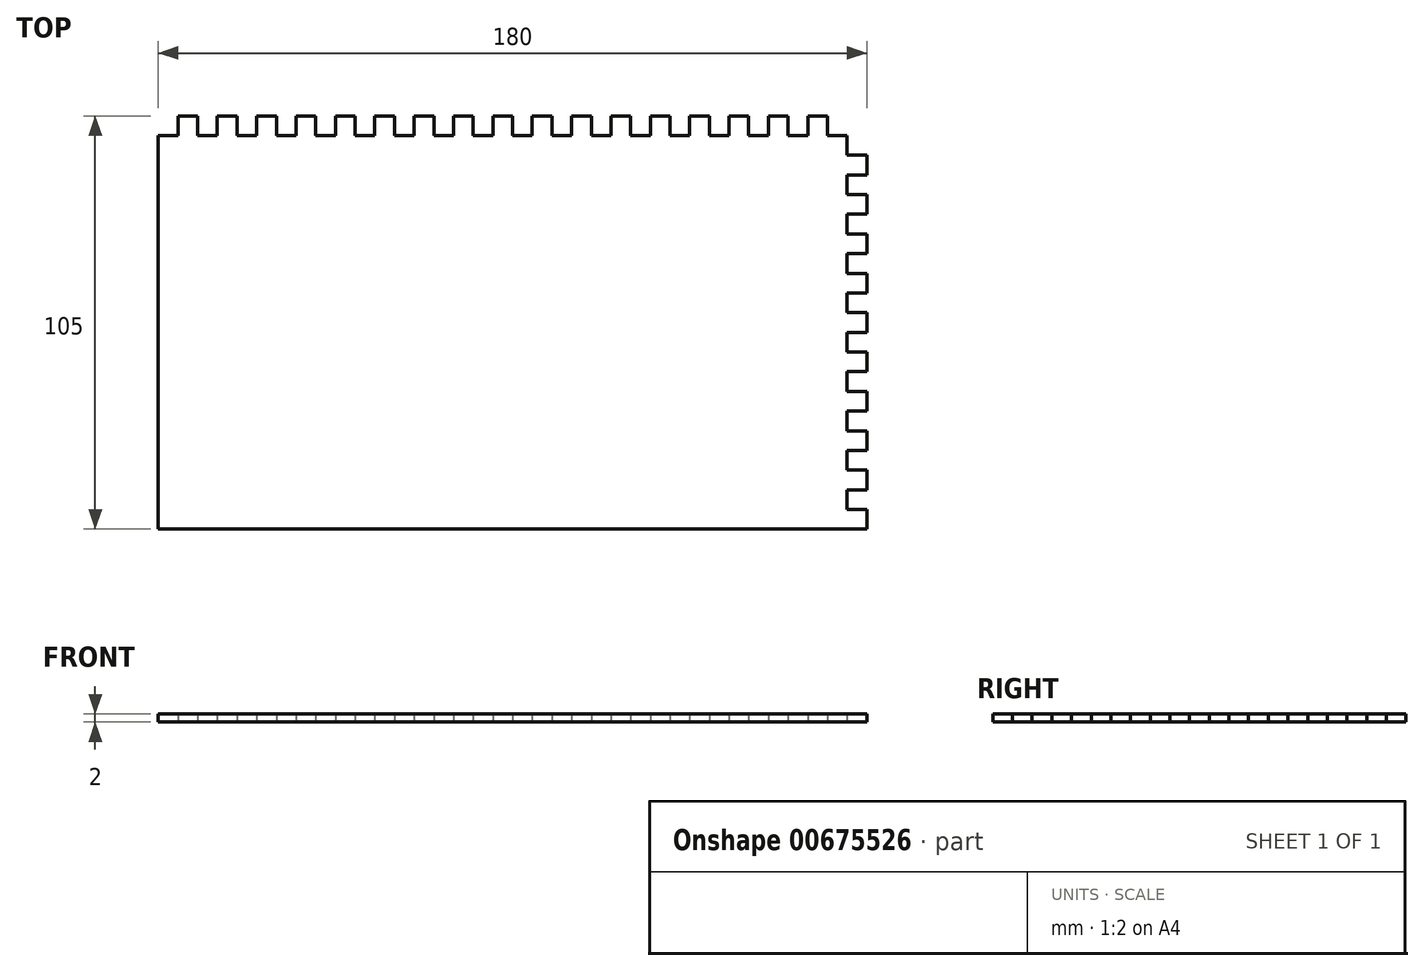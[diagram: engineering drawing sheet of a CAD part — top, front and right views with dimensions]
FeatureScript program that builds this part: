
annotation { "Feature Type Name" : "Feature", "Feature Type Description" : "" }
export const myFeature = defineFeature(function(context is Context, id is Id, definition is map)
    precondition{}
    {
        {
            var Q0;
            Q0=qCreatedBy(makeId("Top.planeOp"),FACE);
            var sketch = newSketch(context, id + "F0", { "sketchPlane" : qUnion([Q0])});
            skLineSegment(sketch, "E0", {"start": v(-180, -103.5) * mm, "end": v(-5, -103.5) * mm});
            skLineSegment(sketch, "E1", {"start": v(-180, -3.5) * mm, "end": v(-180, -103.5) * mm});
            skLineSegment(sketch, "E2", {"start": v(-175, 1.5) * mm, "end": v(-175, -3.5) * mm});
            skLineSegment(sketch, "E3", {"start": v(-170, 1.5) * mm, "end": v(-170, -3.5) * mm});
            skLineSegment(sketch, "E4", {"start": v(-165, 1.5) * mm, "end": v(-165, -3.5) * mm});
            skLineSegment(sketch, "E5", {"start": v(-160, 1.5) * mm, "end": v(-160, -3.5) * mm});
            skLineSegment(sketch, "E6", {"start": v(-155, 1.5) * mm, "end": v(-155, -3.5) * mm});
            skLineSegment(sketch, "E7", {"start": v(-150, 1.5) * mm, "end": v(-150, -3.5) * mm});
            skLineSegment(sketch, "E8", {"start": v(-145, 1.5) * mm, "end": v(-145, -3.5) * mm});
            skLineSegment(sketch, "E9", {"start": v(-140, 1.5) * mm, "end": v(-140, -3.5) * mm});
            skLineSegment(sketch, "E10", {"start": v(-135, 1.5) * mm, "end": v(-135, -3.5) * mm});
            skLineSegment(sketch, "E11", {"start": v(-130, 1.5) * mm, "end": v(-130, -3.5) * mm});
            skLineSegment(sketch, "E12", {"start": v(-125, 1.5) * mm, "end": v(-125, -3.5) * mm});
            skLineSegment(sketch, "E13", {"start": v(-85, 1.5) * mm, "end": v(-85, -3.5) * mm});
            skLineSegment(sketch, "E14", {"start": v(-80, 1.5) * mm, "end": v(-80, -3.5) * mm});
            skLineSegment(sketch, "E15", {"start": v(-75, 1.5) * mm, "end": v(-75, -3.5) * mm});
            skLineSegment(sketch, "E16", {"start": v(-70, 1.5) * mm, "end": v(-70, -3.5) * mm});
            skLineSegment(sketch, "E17", {"start": v(-65, 1.5) * mm, "end": v(-65, -3.5) * mm});
            skLineSegment(sketch, "E18", {"start": v(-60, 1.5) * mm, "end": v(-60, -3.5) * mm});
            skLineSegment(sketch, "E19", {"start": v(-55, 1.5) * mm, "end": v(-55, -3.5) * mm});
            skLineSegment(sketch, "E20", {"start": v(-50, 1.5) * mm, "end": v(-50, -3.5) * mm});
            skLineSegment(sketch, "E21", {"start": v(-45, 1.5) * mm, "end": v(-45, -3.5) * mm});
            skLineSegment(sketch, "E22", {"start": v(-40, 1.5) * mm, "end": v(-40, -3.5) * mm});
            skLineSegment(sketch, "E23", {"start": v(-35, 1.5) * mm, "end": v(-35, -3.5) * mm});
            skLineSegment(sketch, "E24", {"start": v(-30, 1.5) * mm, "end": v(-30, -3.5) * mm});
            skLineSegment(sketch, "E25", {"start": v(-25, 1.5) * mm, "end": v(-25, -3.5) * mm});
            skLineSegment(sketch, "E26", {"start": v(-20, 1.5) * mm, "end": v(-20, -3.5) * mm});
            skLineSegment(sketch, "E27", {"start": v(-15, 1.5) * mm, "end": v(-15, -3.5) * mm});
            skLineSegment(sketch, "E28", {"start": v(-10, 1.5) * mm, "end": v(-10, -3.5) * mm});
            skLineSegment(sketch, "E29", {"start": v(-5, -3.5) * mm, "end": v(-5, -8.5) * mm});
            skLineSegment(sketch, "E30", {"start": v(-5, -8.5) * mm, "end": v(0, -8.5) * mm});
            skLineSegment(sketch, "E31", {"start": v(-5, -13.5) * mm, "end": v(0, -13.5) * mm});
            skLineSegment(sketch, "E32", {"start": v(-5, -18.5) * mm, "end": v(0, -18.5) * mm});
            skLineSegment(sketch, "E33", {"start": v(0, -23.5) * mm, "end": v(-5, -23.5) * mm});
            skLineSegment(sketch, "E34", {"start": v(-5, -28.5) * mm, "end": v(0, -28.5) * mm});
            skLineSegment(sketch, "E35", {"start": v(-5, -33.5) * mm, "end": v(0, -33.5) * mm});
            skLineSegment(sketch, "E36", {"start": v(0, -38.5) * mm, "end": v(-5, -38.5) * mm});
            skLineSegment(sketch, "E37", {"start": v(-5, -43.5) * mm, "end": v(0, -43.5) * mm});
            skLineSegment(sketch, "E38", {"start": v(0, -48.5) * mm, "end": v(-5, -48.5) * mm});
            skLineSegment(sketch, "E39", {"start": v(-5, -53.5) * mm, "end": v(0, -53.5) * mm});
            skLineSegment(sketch, "E40", {"start": v(0, -58.5) * mm, "end": v(-5, -58.5) * mm});
            skLineSegment(sketch, "E41", {"start": v(-5, -63.5) * mm, "end": v(0, -63.5) * mm});
            skLineSegment(sketch, "E42", {"start": v(-5, -68.5) * mm, "end": v(0, -68.5) * mm});
            skLineSegment(sketch, "E43", {"start": v(-5, -73.5) * mm, "end": v(0, -73.5) * mm});
            skLineSegment(sketch, "E44", {"start": v(-5, -78.5) * mm, "end": v(0, -78.5) * mm});
            skLineSegment(sketch, "E45", {"start": v(-5, -83.5) * mm, "end": v(0, -83.5) * mm});
            skLineSegment(sketch, "E46", {"start": v(-5, -88.5) * mm, "end": v(0, -88.5) * mm});
            skLineSegment(sketch, "E47", {"start": v(-5, -93.5) * mm, "end": v(0, -93.5) * mm});
            skLineSegment(sketch, "E48", {"start": v(-5, -98.5) * mm, "end": v(0, -98.5) * mm});
            skLineSegment(sketch, "E49", {"start": v(-120, -3.5) * mm, "end": v(-120, 1.5) * mm});
            skLineSegment(sketch, "E50", {"start": v(-115, 1.5) * mm, "end": v(-115, -3.5) * mm});
            skLineSegment(sketch, "E51", {"start": v(-110, -3.5) * mm, "end": v(-110, 1.5) * mm});
            skLineSegment(sketch, "E52", {"start": v(-105, 1.5) * mm, "end": v(-105, -3.5) * mm});
            skLineSegment(sketch, "E53", {"start": v(-100, 1.5) * mm, "end": v(-100, -3.5) * mm});
            skLineSegment(sketch, "E54", {"start": v(-95, 1.5) * mm, "end": v(-95, -3.5) * mm});
            skLineSegment(sketch, "E55", {"start": v(-90, 1.5) * mm, "end": v(-90, -3.5) * mm});
            skLineSegment(sketch, "E56", {"start": v(-175, 1.5) * mm, "end": v(-170, 1.5) * mm});
            skLineSegment(sketch, "E57", {"start": v(-175, -3.5) * mm, "end": v(-180, -3.5) * mm});
            skLineSegment(sketch, "E58", {"start": v(-170, -3.5) * mm, "end": v(-165, -3.5) * mm});
            skLineSegment(sketch, "E59", {"start": v(-160, 1.5) * mm, "end": v(-165, 1.5) * mm});
            skLineSegment(sketch, "E60", {"start": v(-155, 1.5) * mm, "end": v(-150, 1.5) * mm});
            skLineSegment(sketch, "E61", {"start": v(-145, 1.5) * mm, "end": v(-140, 1.5) * mm});
            skLineSegment(sketch, "E62", {"start": v(-135, 1.5) * mm, "end": v(-130, 1.5) * mm});
            skLineSegment(sketch, "E63", {"start": v(-125, 1.5) * mm, "end": v(-120, 1.5) * mm});
            skLineSegment(sketch, "E64", {"start": v(-125, -3.5) * mm, "end": v(-130, -3.5) * mm});
            skLineSegment(sketch, "E65", {"start": v(-135, -3.5) * mm, "end": v(-140, -3.5) * mm});
            skLineSegment(sketch, "E66", {"start": v(-145, -3.5) * mm, "end": v(-150, -3.5) * mm});
            skLineSegment(sketch, "E67", {"start": v(-155, -3.5) * mm, "end": v(-160, -3.5) * mm});
            skLineSegment(sketch, "E68", {"start": v(-120, -3.5) * mm, "end": v(-115, -3.5) * mm});
            skLineSegment(sketch, "E69", {"start": v(-115, 1.5) * mm, "end": v(-110, 1.5) * mm});
            skLineSegment(sketch, "E70", {"start": v(-110, -3.5) * mm, "end": v(-105, -3.5) * mm});
            skLineSegment(sketch, "E71", {"start": v(-105, 1.5) * mm, "end": v(-100, 1.5) * mm});
            skLineSegment(sketch, "E72", {"start": v(-100, -3.5) * mm, "end": v(-95, -3.5) * mm});
            skLineSegment(sketch, "E73", {"start": v(-95, 1.5) * mm, "end": v(-90, 1.5) * mm});
            skLineSegment(sketch, "E74", {"start": v(-90, -3.5) * mm, "end": v(-85, -3.5) * mm});
            skLineSegment(sketch, "E75", {"start": v(-85, 1.5) * mm, "end": v(-80, 1.5) * mm});
            skLineSegment(sketch, "E76", {"start": v(-80, -3.5) * mm, "end": v(-75, -3.5) * mm});
            skLineSegment(sketch, "E77", {"start": v(-75, 1.5) * mm, "end": v(-70, 1.5) * mm});
            skLineSegment(sketch, "E78", {"start": v(-70, -3.5) * mm, "end": v(-65, -3.5) * mm});
            skLineSegment(sketch, "E79", {"start": v(-65, 1.5) * mm, "end": v(-60, 1.5) * mm});
            skLineSegment(sketch, "E80", {"start": v(-60, -3.5) * mm, "end": v(-55, -3.5) * mm});
            skLineSegment(sketch, "E81", {"start": v(-55, 1.5) * mm, "end": v(-50, 1.5) * mm});
            skLineSegment(sketch, "E82", {"start": v(-50, -3.5) * mm, "end": v(-45, -3.5) * mm});
            skLineSegment(sketch, "E83", {"start": v(-45, 1.5) * mm, "end": v(-40, 1.5) * mm});
            skLineSegment(sketch, "E84", {"start": v(-40, -3.5) * mm, "end": v(-35, -3.5) * mm});
            skLineSegment(sketch, "E85", {"start": v(-35, 1.5) * mm, "end": v(-30, 1.5) * mm});
            skLineSegment(sketch, "E86", {"start": v(-30, -3.5) * mm, "end": v(-25, -3.5) * mm});
            skLineSegment(sketch, "E87", {"start": v(-25, 1.5) * mm, "end": v(-20, 1.5) * mm});
            skLineSegment(sketch, "E88", {"start": v(-20, -3.5) * mm, "end": v(-15, -3.5) * mm});
            skLineSegment(sketch, "E89", {"start": v(-15, 1.5) * mm, "end": v(-10, 1.5) * mm});
            skLineSegment(sketch, "E90", {"start": v(-10, -3.5) * mm, "end": v(-5, -3.5) * mm});
            skLineSegment(sketch, "E91.trimOffspring", {"start": v(-5, -13.5) * mm, "end": v(-5, -18.5) * mm});
            skLineSegment(sketch, "E92", {"start": v(0, -8.5) * mm, "end": v(0, -13.5) * mm});
            skLineSegment(sketch, "E93.trimOffspring", {"start": v(-5, -23.5) * mm, "end": v(-5, -28.5) * mm});
            skLineSegment(sketch, "E94.trimOffspring", {"start": v(-5, -33.5) * mm, "end": v(-5, -38.5) * mm});
            skLineSegment(sketch, "E95.trimOffspring", {"start": v(-5, -43.5) * mm, "end": v(-5, -48.5) * mm});
            skLineSegment(sketch, "E96.trimOffspring", {"start": v(-5, -53.5) * mm, "end": v(-5, -58.5) * mm});
            skLineSegment(sketch, "E97.trimOffspring", {"start": v(-5, -63.5) * mm, "end": v(-5, -68.5) * mm});
            skLineSegment(sketch, "E98", {"start": v(0, -18.5) * mm, "end": v(0, -23.5) * mm});
            skLineSegment(sketch, "E99", {"start": v(0, -28.5) * mm, "end": v(0, -33.5) * mm});
            skLineSegment(sketch, "E100", {"start": v(0, -38.5) * mm, "end": v(0, -43.5) * mm});
            skLineSegment(sketch, "E101", {"start": v(0, -48.5) * mm, "end": v(0, -53.5) * mm});
            skLineSegment(sketch, "E102", {"start": v(0, -58.5) * mm, "end": v(0, -63.5) * mm});
            skLineSegment(sketch, "E103.trimOffspring", {"start": v(-5, -73.5) * mm, "end": v(-5, -78.5) * mm});
            skLineSegment(sketch, "E104.trimOffspring", {"start": v(-5, -83.5) * mm, "end": v(-5, -88.5) * mm});
            skLineSegment(sketch, "E105.trimOffspring", {"start": v(-5, -93.5) * mm, "end": v(-5, -98.5) * mm});
            skLineSegment(sketch, "E106", {"start": v(0, -68.5) * mm, "end": v(0, -73.5) * mm});
            skLineSegment(sketch, "E107", {"start": v(0, -78.5) * mm, "end": v(0, -83.5) * mm});
            skLineSegment(sketch, "E108", {"start": v(0, -88.5) * mm, "end": v(0, -93.5) * mm});
            skLineSegment(sketch, "E109", {"start": v(0, -98.5) * mm, "end": v(0, -103.5) * mm});
            skLineSegment(sketch, "E110", {"start": v(-5, -103.5) * mm, "end": v(0, -103.5) * mm});
            skSolve(sketch);
        }
        {
            var Q0;
            Q0=qSketchRegion(id+"F0",true);
            extrude(context, id + "F1", {"entities" : qUnion([Q0]), "depth" : 2 * mm, "offsetDistance" : 25 * mm});
        }
    });
